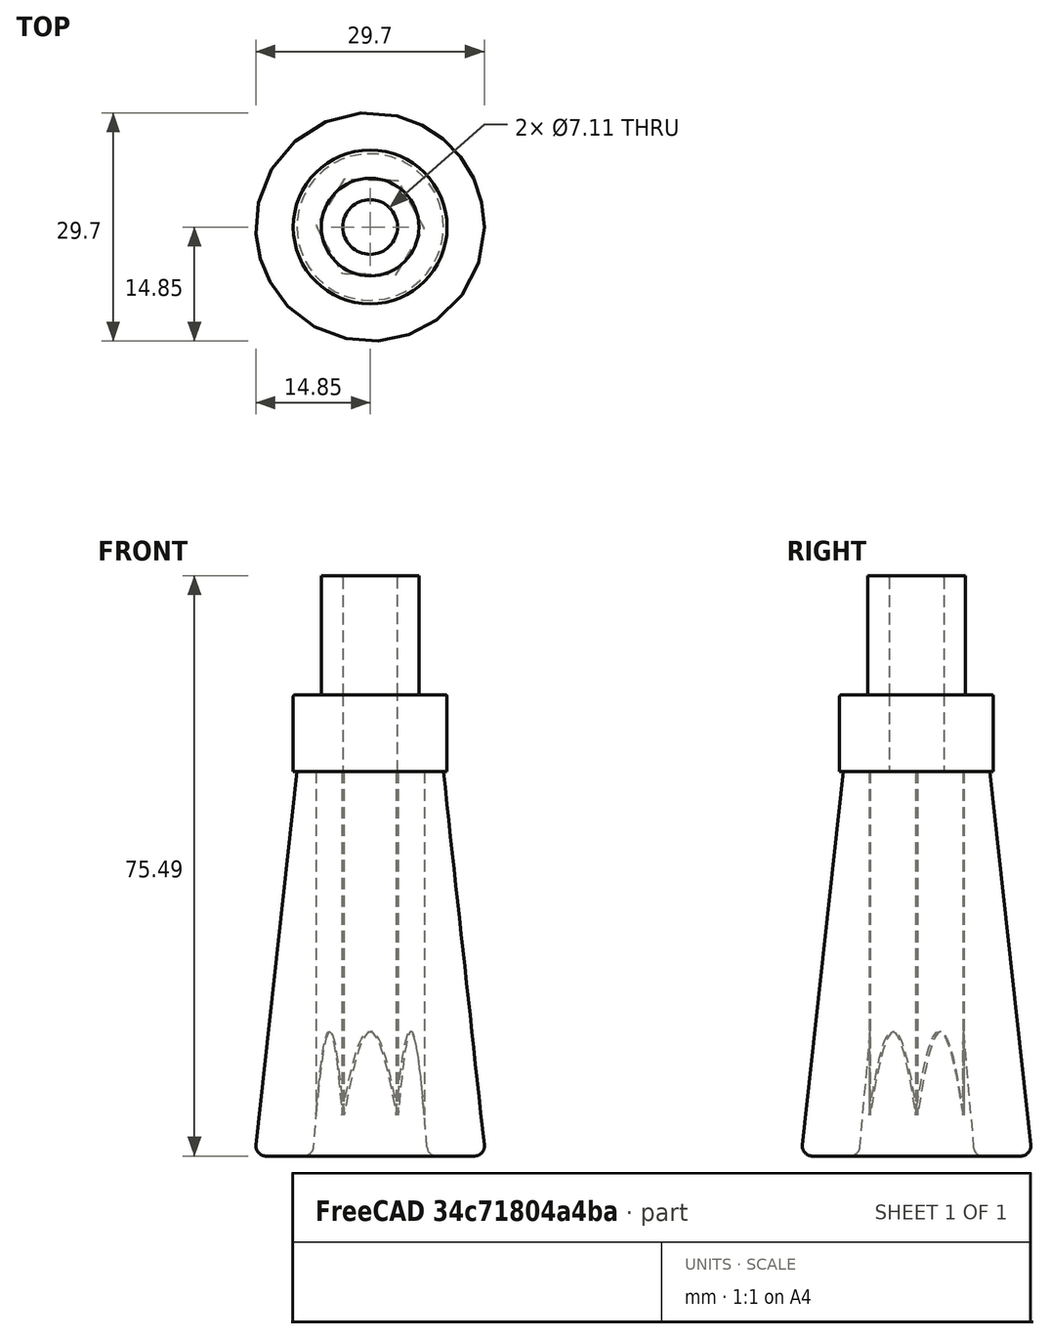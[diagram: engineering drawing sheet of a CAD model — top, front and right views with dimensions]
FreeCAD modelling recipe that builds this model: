
FCSTD DOCUMENT  (FreeCAD 0.19R24291 (Git))
Label: WorkBenchHandle_ForBnD__0_25x20Bolt
License: All rights reserved
LicenseURL: http://en.wikipedia.org/wiki/All_rights_reserved
objects: TechDraw::DrawViewDimension×10, Sketcher::SketchObject×7, TechDraw::DrawProjGroupItem×4, PartDesign::Pocket×3, PartDesign::Fillet×3, PartDesign::Pad×2, TechDraw::DrawSVGTemplate×1, PartDesign::AdditiveLoft×1, PartDesign::Body×1, TechDraw::DrawProjGroup×1, TechDraw::DrawPage×1
note: 26 computed .brp shape members not serialized (recipe doc carries the construction recipe); baked Part::Feature solids carry a one-line shape summary decoded from their .brp

FEATURE [TechDraw::DrawSVGTemplate] Template
  EditableTexts = Approved1=Approved 1; Approved2=Approved 2; CheckedBy=on 20230706; Code=Code; CompanyAddress=3433 Riegeway Trail; CompanyName=Amused Scientist; DrawingNumber=Drawing Number; DrawingTitle1=WorkBenchHandle_Hex_BnD; DrawingTitle2=Drawing Title 2; DrawingTitle3=Drawing Title 3; DrawnBy=Lee Erickson; Revision=Rev; Scale=Scale 1:1; Sheet=Sheet n of m
  Height = 215.9
  Orientation = 1
  Width = 279.4
FEATURE [Sketcher::SketchObject] Sketch
  FullyConstrained = true
  MapMode = 5
  Support = -> [XY_Plane]
  sketch-geometry (2):
    g0: Circle CenterX=0 CenterY=0 CenterZ=0 NormalX=0 NormalY=0 NormalZ=1 AngleXU=0 Radius=15
    g1: Circle CenterX=0 CenterY=0 CenterZ=0 NormalX=0 NormalY=0 NormalZ=1 AngleXU=0 Radius=7.5
  constraints (4):
    c: Coincident(g0,g-1)
    c: Coincident(g1,g0)
    c: Diameter(g0) = 30
    c: Diameter(g1) = 15
FEATURE [Sketcher::SketchObject] Sketch001
  AttachmentOffset = pos=(0,0,50) rot=(0,0,1;0rad)
  FullyConstrained = true
  MapMode = 5
  Placement = pos=(0,0,50) rot=(0,0,1;0rad)
  Support = -> [XY_Plane]
  sketch-geometry (2):
    g0: Circle CenterX=0 CenterY=0 CenterZ=0 NormalX=0 NormalY=0 NormalZ=1 AngleXU=0 Radius=9.525
    g1: Circle CenterX=0 CenterY=0 CenterZ=0 NormalX=0 NormalY=0 NormalZ=1 AngleXU=0 Radius=3.175
  constraints (4):
    c: Coincident(g0,g-1)
    c: Coincident(g1,g0)
    c: Diameter(g0) = 19.05
    c: Diameter(g1) = 6.35
FEATURE [PartDesign::AdditiveLoft] AdditiveLoft  label="AdditiveLoftHandel"
  Closed = false
  Profile = -> Sketch
  Ruled = false
  Sections = -> [Sketch001]
FEATURE [Sketcher::SketchObject] Sketch002
  FullyConstrained = true
  MapMode = 5
  Placement = pos=(0,0,50) rot=(0,0,1;0rad)
  Support = -> [AdditiveLoft]
  sketch-geometry (1):
    g0: Circle CenterX=0 CenterY=0 CenterZ=0 NormalX=0 NormalY=0 NormalZ=1 AngleXU=0 Radius=10
  constraints (2):
    c: Coincident(g0,g-1)
    c: Diameter(g0) = 20
FEATURE [PartDesign::Pad] Pad  label="PadBoss"
  BaseFeature = -> AdditiveLoft
  Direction = (1,1,1)
  Length = 10
  Length2 = 100
  Profile = -> Sketch002
  Type = 0
FEATURE [Sketcher::SketchObject] Sketch003
  FullyConstrained = true
  MapMode = 5
  Support = -> [XY_Plane]
  sketch-geometry (1):
    g0: Circle CenterX=0 CenterY=0 CenterZ=0 NormalX=0 NormalY=0 NormalZ=1 AngleXU=0 Radius=3.556
  constraints (2):
    c: Coincident(g0,g-1)
    c: Diameter(g0) = 7.112
FEATURE [Sketcher::SketchObject] Sketch004
  FullyConstrained = false
  MapMode = 5
  Placement = pos=(0,0,50) rot=(0,0,1;0rad)
  Support = -> [AdditiveLoft]
  sketch-geometry (7):
    g0: LineSegment StartX=7.03749 StartY=-0.148514 StartZ=0 EndX=3.64736 EndY=6.02039 EndZ=0
    g1: LineSegment StartX=3.64736 StartY=6.02039 StartZ=0 EndX=-3.39013 EndY=6.1689 EndZ=0
    g2: LineSegment StartX=-3.39013 StartY=6.1689 StartZ=0 EndX=-7.03749 EndY=0.148514 EndZ=0
    g3: LineSegment StartX=-7.03749 StartY=0.148514 StartZ=0 EndX=-3.64736 EndY=-6.02039 EndZ=0
    g4: LineSegment StartX=-3.64736 StartY=-6.02039 StartZ=0 EndX=3.39013 EndY=-6.1689 EndZ=0
    g5: LineSegment StartX=3.39013 StartY=-6.1689 StartZ=0 EndX=7.03749 EndY=-0.148514 EndZ=0
    g6: Circle CenterX=0 CenterY=0 CenterZ=0 NormalX=0 NormalY=0 NormalZ=1 AngleXU=0 Radius=7.03905
  constraints (15):
    c: Coincident(g0,g1)
    c: Coincident(g1,g2)
    c: Coincident(g2,g3)
    c: Coincident(g3,g4)
    c: Coincident(g4,g5)
    c: Coincident(g5,g0)
    c: Equal(g0, g1-g5) x5
    c: PointOnObject(g0,g6)
    c: PointOnObject(g1,g6)
    c: PointOnObject(g2,g6)
    c: PointOnObject(g3,g6)
    c: PointOnObject(g4,g6)
    c: PointOnObject(g5,g6)
    c: Coincident(g6,g-1)
    c: Distance(g1,g0) = 12.192
FEATURE [Sketcher::SketchObject] Sketch006
  FullyConstrained = true
  MapMode = 5
  Support = -> [XY_Plane]
  sketch-geometry (1):
    g0: Circle CenterX=0 CenterY=0 CenterZ=0 NormalX=0 NormalY=0 NormalZ=1 AngleXU=0 Radius=3.556
  constraints (2):
    c: Coincident(g0,g-1)
    c: Diameter(g0) = 7.112
FEATURE [PartDesign::Pocket] Pocket  label="PocketBoltHole"
  BaseFeature = -> Pad
  Length = 5.08
  Length2 = 100.076
  Profile = -> Sketch003
  Reversed = true
  Type = 1
FEATURE [PartDesign::Pocket] Pocket001  label="PocketHex"
  BaseFeature = -> Pocket
  Length = 5.08
  Length2 = 100.076
  Profile = -> Sketch004
  Type = 1
FEATURE [Sketcher::SketchObject] Sketch005
  FullyConstrained = true
  MapMode = 5
  Placement = pos=(0,0,60) rot=(0,0,1;0rad)
  Support = -> [Pocket001]
  sketch-geometry (1):
    g0: Circle CenterX=0 CenterY=0 CenterZ=0 NormalX=0 NormalY=0 NormalZ=1 AngleXU=0 Radius=6.35
  constraints (2):
    c: Coincident(g0,g-1)
    c: Diameter(g0) = 12.7
FEATURE [PartDesign::Pad] Pad001  label="PadPin"
  BaseFeature = -> Pocket001
  Direction = (1,1,1)
  Length = 15.494
  Length2 = 100.076
  Profile = -> Sketch005
  Type = 0
FEATURE [PartDesign::Pocket] Pocket002  label="PocketBotlHole2"
  BaseFeature = -> Pad001
  Length = 5.08
  Length2 = 100.076
  Profile = -> Sketch006
  Reversed = true
  Type = 1
FEATURE [PartDesign::Fillet] Fillet
  Base = -> Pocket002 [Edge10,Edge6]
  BaseFeature = -> Pocket002
  Radius = 1.27
  SupportTransform = false
FEATURE [PartDesign::Fillet] Fillet001
  Base = -> Fillet [Edge9]
  BaseFeature = -> Fillet
  Radius = 0.254
  SupportTransform = false
FEATURE [PartDesign::Fillet] Fillet002
  Base = -> Fillet001 [Edge14]
  BaseFeature = -> Fillet001
  Radius = 0.254
  SupportTransform = false
FEATURE [PartDesign::Body] Body
  Group = -> [Sketch,Sketch001,AdditiveLoft,Sketch002,Pad,Sketch003,Pocket,Sketch004,Pocket001,Sketch005,Pad001,Sketch006,Pocket002,Fillet,Fillet001,Fillet002]
  Origin = -> Origin
  Tip = -> Fillet002
FEATURE [TechDraw::DrawProjGroupItem] ProjItem  label="Front"
  CoarseView = false
  Direction = (0,0,1)
  Focus = 100
  HardHidden = false
  IsoCount = 0
  IsoHidden = false
  IsoVisible = false
  LockPosition = true
  Perspective = false
  Rotation = 0
  RotationVector = (1,0,0)
  ScaleType = 2
  SeamHidden = false
  SeamVisible = false
  SmoothHidden = false
  SmoothVisible = false
  Source = -> [Body]
  Type = 0
  X = 0
  XDirection = (1,0,0)
  Y = 0
FEATURE [TechDraw::DrawProjGroupItem] ProjItem001  label="Left"
  CoarseView = false
  Direction = (-1,0,1e-16)
  Focus = 100
  HardHidden = false
  IsoCount = 0
  IsoHidden = false
  IsoVisible = false
  LockPosition = true
  Perspective = false
  Rotation = 0
  RotationVector = (1,0,0)
  ScaleType = 2
  SeamHidden = false
  SeamVisible = false
  SmoothHidden = false
  SmoothVisible = false
  Source = -> [Body]
  Type = 1
  X = 90.48
  XDirection = (1e-16,0,1)
  Y = 0
FEATURE [TechDraw::DrawProjGroupItem] ProjItem002  label="FrontTopRight"
  CoarseView = false
  Direction = (0.57735,0.57735,0.57735)
  Focus = 100
  HardHidden = false
  IsoCount = 0
  IsoHidden = false
  IsoVisible = false
  LockPosition = true
  Perspective = false
  Rotation = 0
  RotationVector = (1,0,0)
  ScaleType = 2
  SeamHidden = false
  SeamVisible = false
  SmoothHidden = false
  SmoothVisible = false
  Source = -> [Body]
  Type = 7
  X = 149.267
  XDirection = (0.707107,0,-0.707107)
  Y = 66.7721
FEATURE [TechDraw::DrawProjGroupItem] ProjItem003  label="Rear"
  CoarseView = false
  Direction = (0,0,-1)
  Focus = 100
  HardHidden = false
  IsoCount = 0
  IsoHidden = false
  IsoVisible = false
  LockPosition = true
  Perspective = false
  Rotation = 0
  RotationVector = (1,0,0)
  ScaleType = 2
  SeamHidden = false
  SeamVisible = false
  SmoothHidden = false
  SmoothVisible = false
  Source = -> [Body]
  Type = 3
  X = 180.96
  XDirection = (-1,0,0)
  Y = 0
FEATURE [TechDraw::DrawProjGroup] ProjGroup
  Anchor = -> ProjItem
  AutoDistribute = true
  LockPosition = false
  ProjectionType = 0
  Rotation = 0
  ScaleType = 0
  Source = -> [Body]
  Views = -> [ProjItem,ProjItem001,ProjItem002,ProjItem003]
  X = 44.9372
  Y = 100.387
  spacingX = 14.986
  spacingY = 14.986
FEATURE [TechDraw::DrawViewDimension] Dimension
  Arbitrary = false
  ArbitraryTolerances = false
  EqualTolerance = true
  FormatSpec = ⌀%.2f
  FormatSpecOverTolerance = %+.2f
  FormatSpecUnderTolerance = %+.2f
  Inverted = false
  LockPosition = false
  MeasureType = 1
  OverTolerance = 0
  References2D = -> [ProjItem]
  Rotation = 0
  ScaleType = 0
  TheoreticalExact = false
  Type = 5
  UnderTolerance = 0
  X = 47.7439
  Y = 33.0428
FEATURE [TechDraw::DrawViewDimension] Dimension001
  Arbitrary = false
  ArbitraryTolerances = false
  EqualTolerance = true
  FormatSpec = ⌀%.2f
  FormatSpecOverTolerance = %+.2f
  FormatSpecUnderTolerance = %+.2f
  Inverted = false
  LockPosition = false
  MeasureType = 1
  OverTolerance = 0
  References2D = -> [ProjItem]
  Rotation = 0
  ScaleType = 0
  TheoreticalExact = false
  Type = 5
  UnderTolerance = 0
  X = 40.5261
  Y = 40.6894
FEATURE [TechDraw::DrawViewDimension] Dimension002
  Arbitrary = false
  ArbitraryTolerances = false
  EqualTolerance = true
  FormatSpec = ⌀%.2f
  FormatSpecOverTolerance = %+.2f
  FormatSpecUnderTolerance = %+.2f
  Inverted = false
  LockPosition = false
  MeasureType = 1
  OverTolerance = 0
  References2D = -> [ProjItem]
  Rotation = 0
  ScaleType = 0
  TheoreticalExact = false
  Type = 5
  UnderTolerance = 0
  X = 32.829
  Y = 48.059
FEATURE [TechDraw::DrawViewDimension] Dimension003
  Arbitrary = false
  ArbitraryTolerances = false
  EqualTolerance = true
  FormatSpec = ⌀%.2f
  FormatSpecOverTolerance = %+.2f
  FormatSpecUnderTolerance = %+.2f
  Inverted = false
  LockPosition = false
  MeasureType = 1
  OverTolerance = 0
  References2D = -> [ProjItem]
  Rotation = 0
  ScaleType = 0
  TheoreticalExact = false
  Type = 5
  UnderTolerance = 0
  X = 19.7834
  Y = 52.8059
FEATURE [TechDraw::DrawViewDimension] Dimension004
  Arbitrary = false
  ArbitraryTolerances = false
  EqualTolerance = true
  FormatSpec = %.2f
  FormatSpecOverTolerance = %+.2f
  FormatSpecUnderTolerance = %+.2f
  Inverted = false
  LockPosition = false
  MeasureType = 1
  OverTolerance = 0
  References2D = -> [ProjItem001]
  Rotation = 0
  ScaleType = 0
  TheoreticalExact = false
  Type = 1
  UnderTolerance = 0
  X = -10.0395
  Y = 23.4311
FEATURE [TechDraw::DrawViewDimension] Dimension006
  Arbitrary = false
  ArbitraryTolerances = false
  EqualTolerance = true
  FormatSpec = %.2f
  FormatSpecOverTolerance = %+.2f
  FormatSpecUnderTolerance = %+.2f
  Inverted = false
  LockPosition = false
  MeasureType = 1
  OverTolerance = 0
  References2D = -> [ProjItem001]
  Rotation = 0
  ScaleType = 0
  TheoreticalExact = false
  Type = 1
  UnderTolerance = 0
  X = -7.7834
  Y = 31.072
FEATURE [TechDraw::DrawViewDimension] Dimension007
  Arbitrary = false
  ArbitraryTolerances = false
  EqualTolerance = true
  FormatSpec = %.2f
  FormatSpecOverTolerance = %+.2f
  FormatSpecUnderTolerance = %+.2f
  Inverted = false
  LockPosition = false
  MeasureType = 1
  OverTolerance = 0
  References2D = -> [ProjItem001]
  Rotation = 0
  ScaleType = 0
  TheoreticalExact = false
  Type = 2
  UnderTolerance = 0
  X = 42.4652
  Y = 21.2317
FEATURE [TechDraw::DrawViewDimension] Dimension009
  Arbitrary = false
  ArbitraryTolerances = false
  EqualTolerance = true
  FormatSpec = %.2f
  FormatSpecOverTolerance = %+.2f
  FormatSpecUnderTolerance = %+.2f
  Inverted = false
  LockPosition = false
  MeasureType = 1
  OverTolerance = 0
  References2D = -> [ProjItem001]
  Rotation = 0
  ScaleType = 0
  TheoreticalExact = false
  Type = 1
  UnderTolerance = 0
  X = 36.5767
  Y = 35.3923
FEATURE [TechDraw::DrawViewDimension] Dimension010
  Arbitrary = false
  ArbitraryTolerances = false
  EqualTolerance = true
  FormatSpec = %.2f
  FormatSpecOverTolerance = %+.2f
  FormatSpecUnderTolerance = %+.2f
  Inverted = false
  LockPosition = false
  MeasureType = 1
  OverTolerance = 0
  References2D = -> [ProjItem001]
  Rotation = 0
  ScaleType = 0
  TheoreticalExact = false
  Type = 2
  UnderTolerance = 0
  X = 52.932
  Y = 21.5008
FEATURE [TechDraw::DrawViewDimension] Dimension011
  Arbitrary = false
  ArbitraryTolerances = false
  EqualTolerance = true
  FormatSpec = %.2f
  FormatSpecOverTolerance = %+.2f
  FormatSpecUnderTolerance = %+.2f
  Inverted = false
  LockPosition = false
  MeasureType = 1
  OverTolerance = 0
  References2D = -> [ProjItem003]
  Rotation = 0
  ScaleType = 0
  TheoreticalExact = false
  Type = 2
  UnderTolerance = 0
  X = 17.8822
  Y = 25.2272
FEATURE [TechDraw::DrawPage] Page  label="PageHandel"
  KeepUpdated = true
  NextBalloonIndex = 1
  ProjectionType = 0
  Template = -> Template
  Views = -> [ProjGroup,Dimension,Dimension001,Dimension002,Dimension003,Dimension004,Dimension006,Dimension007,Dimension009,Dimension010,Dimension011]
